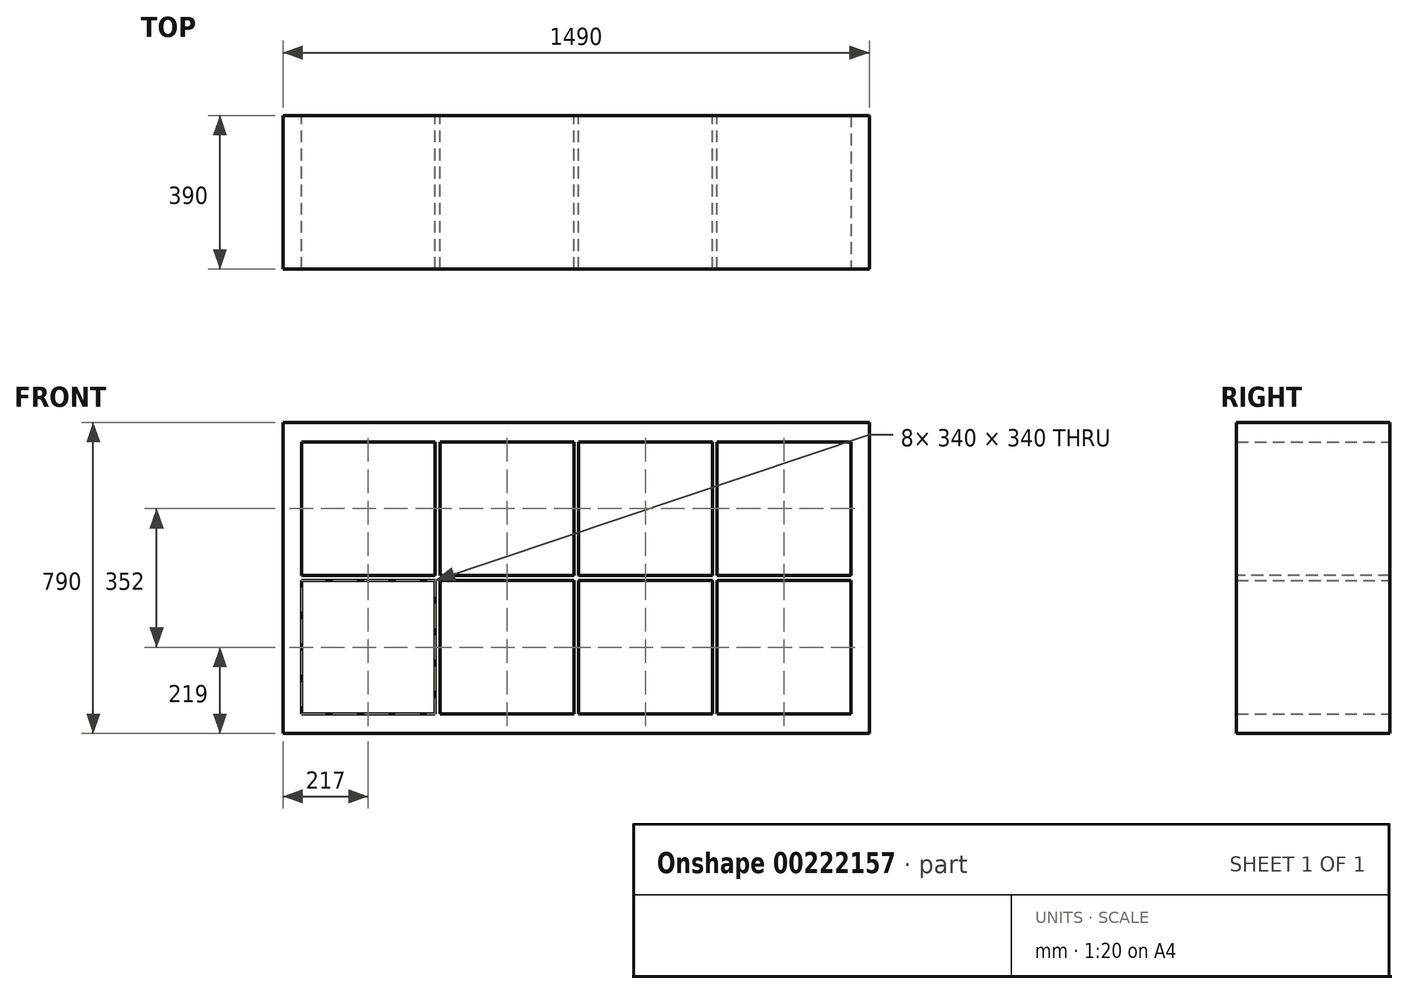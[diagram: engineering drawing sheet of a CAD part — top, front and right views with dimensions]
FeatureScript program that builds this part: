
annotation { "Feature Type Name" : "Feature", "Feature Type Description" : "" }
export const myFeature = defineFeature(function(context is Context, id is Id, definition is map)
    precondition{}
    {
        {
            var Q0;
            Q0=qCreatedBy(makeId("Top.planeOp"),FACE);
            var sketch = newSketch(context, id + "F0", { "sketchPlane" : qUnion([Q0])});
            skLineSegment(sketch, "E0.bottom", {"start": v(745, -195) * mm, "end": v(-745, -195) * mm});
            skLineSegment(sketch, "E0.top", {"start": v(745, 195) * mm, "end": v(-745, 195) * mm});
            skLineSegment(sketch, "E0.left", {"start": v(745, -195) * mm, "end": v(745, 195) * mm});
            skLineSegment(sketch, "E0.right", {"start": v(-745, -195) * mm, "end": v(-745, 195) * mm});
            skPoint(sketch, "E0.middle", {"position": v(0, 0) * mm});
            skSolve(sketch);
        }
        {
            var Q0;
            Q0 = qSketchRegion(id + "F0", true);
            extrude(context, id + "F1", {"entities" : qUnion([Q0]), "depth" : 49 * mm});
        }
        {
            var Q0;
            Q0=makeQuery(id+"F1.opExtrude","CAP_FACE",FACE,{"disambiguationData":[OSD([sQuery(id+"F0.wireOp",EDGE,"E0.bottom"),sQuery(id+"F0.wireOp",EDGE,"E0.top"),sQuery(id+"F0.wireOp",EDGE,"E0.left"),sQuery(id+"F0.wireOp",EDGE,"E0.right")])],"isStart":false});
            var sketch = newSketch(context, id + "F2", { "sketchPlane" : qUnion([Q0])});
            skLineSegment(sketch, "E1.bottom", {"start": v(-745, -195) * mm, "end": v(-698, -195) * mm});
            skLineSegment(sketch, "E1.top", {"start": v(-745, 195) * mm, "end": v(-698, 195) * mm});
            skLineSegment(sketch, "E1.left", {"start": v(-745, -195) * mm, "end": v(-745, 195) * mm});
            skLineSegment(sketch, "E1.right", {"start": v(-698, -195) * mm, "end": v(-698, 195) * mm});
            skLineSegment(sketch, "E2.bottom", {"start": v(745, -195) * mm, "end": v(698, -195) * mm});
            skLineSegment(sketch, "E2.top", {"start": v(745, 195) * mm, "end": v(698, 195) * mm});
            skLineSegment(sketch, "E2.left", {"start": v(745, -195) * mm, "end": v(745, 195) * mm});
            skLineSegment(sketch, "E2.right", {"start": v(698, -195) * mm, "end": v(698, 195) * mm});
            skLineSegment(sketch, "E3.bottom", {"start": v(358, -195) * mm, "end": v(346, -195) * mm});
            skLineSegment(sketch, "E3.top", {"start": v(358, 195) * mm, "end": v(346, 195) * mm});
            skLineSegment(sketch, "E3.left", {"start": v(358, -195) * mm, "end": v(358, 195) * mm});
            skLineSegment(sketch, "E3.right", {"start": v(346, -195) * mm, "end": v(346, 195) * mm});
            skLineSegment(sketch, "E4.bottom", {"start": v(6, -195) * mm, "end": v(-6, -195) * mm});
            skLineSegment(sketch, "E4.top", {"start": v(6, 195) * mm, "end": v(-6, 195) * mm});
            skLineSegment(sketch, "E4.left", {"start": v(6, -195) * mm, "end": v(6, 195) * mm});
            skLineSegment(sketch, "E4.right", {"start": v(-6, -195) * mm, "end": v(-6, 195) * mm});
            skLineSegment(sketch, "E5.bottom", {"start": v(-346, -195) * mm, "end": v(-358, -195) * mm});
            skLineSegment(sketch, "E5.top", {"start": v(-346, 195) * mm, "end": v(-358, 195) * mm});
            skLineSegment(sketch, "E5.left", {"start": v(-346, -195) * mm, "end": v(-346, 195) * mm});
            skLineSegment(sketch, "E5.right", {"start": v(-358, -195) * mm, "end": v(-358, 195) * mm});
            skSolve(sketch);
        }
        {
            var Q0;
            Q0 = qSketchRegion(id + "F2", true);
            extrude(context, id + "F3", {"entities" : qUnion([Q0]), "operationType" : NewBodyOperationType.ADD, "depth" : 692 * mm});
        }
        {
            var Q0;
            Q0=makeQuery(id+"F3.opExtrude","CAP_FACE",FACE,{"disambiguationData":[OSD([sQuery(id+"F2.wireOp",EDGE,"E1.bottom"),sQuery(id+"F2.wireOp",EDGE,"E1.top"),sQuery(id+"F2.wireOp",EDGE,"E1.left"),sQuery(id+"F2.wireOp",EDGE,"E1.right")])],"isStart":false});
            var sketch = newSketch(context, id + "F4", { "sketchPlane" : qUnion([Q0])});
            skLineSegment(sketch, "E6.bottom", {"start": v(-745, -195) * mm, "end": v(745, -195) * mm});
            skLineSegment(sketch, "E6.top", {"start": v(-745, 195) * mm, "end": v(745, 195) * mm});
            skLineSegment(sketch, "E6.left", {"start": v(-745, -195) * mm, "end": v(-745, 195) * mm});
            skLineSegment(sketch, "E6.right", {"start": v(745, -195) * mm, "end": v(745, 195) * mm});
            skSolve(sketch);
        }
        {
            var Q0;
            Q0 = qSketchRegion(id + "F4", true);
            extrude(context, id + "F5", {"entities" : qUnion([Q0]), "operationType" : NewBodyOperationType.ADD, "depth" : 49 * mm});
        }
        {
            var Q0;
            Q0=makeQuery(id+"F3.opExtrude","SWEPT_FACE",FACE,{"disambiguationData":[OSD([sQuery(id+"F2.wireOp",EDGE,"E2.right")])]});
            var sketch = newSketch(context, id + "F6", { "sketchPlane" : qUnion([Q0])});
            skLineSegment(sketch, "E7.bottom", {"start": v(-195, 401) * mm, "end": v(195, 401) * mm});
            skLineSegment(sketch, "E7.top", {"start": v(-195, 389) * mm, "end": v(195, 389) * mm});
            skLineSegment(sketch, "E7.left", {"start": v(-195, 401) * mm, "end": v(-195, 389) * mm});
            skLineSegment(sketch, "E7.right", {"start": v(195, 401) * mm, "end": v(195, 389) * mm});
            skSolve(sketch);
        }
        {
            var Q0;
            Q0 = qSketchRegion(id + "F6", true);
            extrude(context, id + "F7", {"entities" : qUnion([Q0]), "operationType" : NewBodyOperationType.ADD, "depth" : 1410 * mm});
        }
    });
